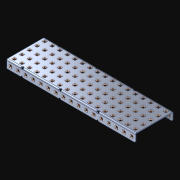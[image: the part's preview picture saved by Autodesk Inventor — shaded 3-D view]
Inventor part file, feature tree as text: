
AUTODESK INVENTOR PART (.ipt)
format: ipt  version: 2021 (Build 250183000, 183)  size: 1,876,480 bytes
history: native  units: in
note: dims shown in document units (in); Inventor stores cm internally (conversion verified against a paired STEP export)
features: extrude x120, other x120, sketch x4, pattern_linear x3
ambient origin geometry x8: Origin, YZ Plane, XZ Plane, XY Plane, X Axis, Y Axis, Z Axis, Center Point
bodies: Solid1 (feature_tree)
feature tree (247):
  pattern_linear  "Rectangular Pattern1"  Spacing1=0.182in  [1 undecoded]
  pattern_linear  "Rectangular Pattern2"  Spacing1=0.046in  [1 undecoded]
  pattern_linear  "Rectangular Pattern3"  Spacing1=0.5in  [1 undecoded]
  extrude  "Extrusion1"  Depth=0.046in
  sketch  "Sketch1"  dims[d0=0.182in]
  other  "Srf1"
  sketch  "Sketch2"  dims[d1=0.046in d2=0.0in]
  other  "Srf2"
  sketch  "Sketch3"  dims[d3=0.182in]
  other  "Srf3"
  other  "Srf4"
  other  "Srf5"
  other  "Srf6"
  other  "Srf7"
  other  "Srf8"
  other  "Srf9"
  other  "Srf10"
  other  "Srf11"
  other  "Srf12"
  other  "Srf13"
  other  "Srf14"
  other  "Srf15"
  other  "Srf16"
  other  "Srf17"
  other  "Srf18"
  other  "Srf19"
  other  "Srf38"
  other  "Srf39"
  other  "Srf40"
  other  "Srf41"
  other  "Srf42"
  other  "Srf43"
  other  "Srf44"
  other  "Srf45"
  other  "Srf46"
  other  "Srf47"
  other  "Srf48"
  other  "Srf49"
  other  "Srf50"
  other  "Srf51"
  other  "Srf52"
  other  "Srf53"
  other  "Srf72"
  other  "Srf73"
  other  "Srf74"
  other  "Srf75"
  other  "Srf76"
  other  "Srf77"
  other  "Srf78"
  other  "Srf79"
  other  "Srf80"
  other  "Srf81"
  other  "Srf82"
  other  "Srf83"
  other  "Srf84"
  other  "Srf85"
  other  "Srf86"
  other  "Srf87"
  other  "Srf88"
  other  "Srf107"
  other  "Srf108"
  other  "Srf109"
  other  "Srf110"
  other  "Srf111"
  other  "Srf112"
  other  "Srf113"
  other  "Srf114"
  other  "Srf115"
  other  "Srf116"
  other  "Srf117"
  other  "Srf118"
  other  "Srf119"
  other  "Srf120"
  other  "Srf121"
  other  "Srf122"
  other  "Srf123"
  other  "Srf142"
  other  "Srf143"
  other  "Srf144"
  other  "Srf145"
  other  "Srf146"
  other  "Srf147"
  other  "Srf148"
  other  "Srf149"
  other  "Srf150"
  other  "Srf151"
  other  "Srf152"
  other  "Srf153"
  other  "Srf154"
  other  "Srf155"
  other  "Srf156"
  other  "Srf157"
  other  "Srf158"
  other  "Srf177"
  other  "Srf178"
  other  "Srf179"
  other  "Srf180"
  other  "Srf181"
  other  "Srf182"
  other  "Srf183"
  other  "Srf184"
  other  "Srf185"
  other  "Srf186"
  other  "Srf187"
  other  "Srf188"
  other  "Srf189"
  other  "Srf190"
  other  "Srf191"
  other  "Srf192"
  other  "Srf193"
  other  "Srf212"
  other  "Srf213"
  other  "Srf214"
  other  "Srf215"
  other  "Srf216"
  other  "Srf217"
  other  "Srf218"
  other  "Srf219"
  other  "Srf220"
  other  "Srf221"
  other  "Srf222"
  other  "Srf223"
  other  "Srf224"
  other  "Srf225"
  other  "Srf226"
  other  "Srf227"
  sketch  "Sketch4"  dims[d4=0.046in d5=0.0in d6=0.182in d7=0.046in d8=0.0in d11=0.5in d12=6.6929in d14=0.5in d15=1.9685in d17=0.5in d18=6.6929in d20=0.5in d21=9.0in d22=0.0in]
  parser-record x1  (decoder bookkeeping rows leaked as tree rows — omitted from the tree; the rows remain in map.json)
  extrude  "ExtrusionSrf1"  Depth=0.046in
  extrude  "ExtrusionSrf2"  Depth=0.046in
  extrude  "ExtrusionSrf3"  Depth=0.046in
  extrude  "ExtrusionSrf4"  Depth=0.046in
  extrude  "ExtrusionSrf5"  Depth=0.046in
  extrude  "ExtrusionSrf6"  TaperAngle=0.0deg  [1 undecoded]
  extrude  "ExtrusionSrf7"  [1 undecoded]
  extrude  "ExtrusionSrf8"  [1 undecoded]
  extrude  "ExtrusionSrf9"  [1 undecoded]
  extrude  "ExtrusionSrf10"  [1 undecoded]
  extrude  "ExtrusionSrf11"  [1 undecoded]
  extrude  "ExtrusionSrf12"  [1 undecoded]
  extrude  "ExtrusionSrf13"  [1 undecoded]
  extrude  "ExtrusionSrf14"  [1 undecoded]
  extrude  "ExtrusionSrf15"  [1 undecoded]
  extrude  "ExtrusionSrf16"  [1 undecoded]
  extrude  "ExtrusionSrf17"  [1 undecoded]
  extrude  "ExtrusionSrf18"  [1 undecoded]
  extrude  "ExtrusionSrf19"  [1 undecoded]
  extrude  "ExtrusionSrf38"  [1 undecoded]
  extrude  "ExtrusionSrf39"  [1 undecoded]
  extrude  "ExtrusionSrf40"  [1 undecoded]
  extrude  "ExtrusionSrf41"  [1 undecoded]
  extrude  "ExtrusionSrf42"  [1 undecoded]
  extrude  "ExtrusionSrf43"  [1 undecoded]
  extrude  "ExtrusionSrf44"  [1 undecoded]
  extrude  "ExtrusionSrf45"  [1 undecoded]
  extrude  "ExtrusionSrf46"  [1 undecoded]
  extrude  "ExtrusionSrf47"  [1 undecoded]
  extrude  "ExtrusionSrf48"  [1 undecoded]
  extrude  "ExtrusionSrf49"  [1 undecoded]
  extrude  "ExtrusionSrf50"  [1 undecoded]
  extrude  "ExtrusionSrf51"  [1 undecoded]
  extrude  "ExtrusionSrf52"  [1 undecoded]
  extrude  "ExtrusionSrf53"  [1 undecoded]
  extrude  "ExtrusionSrf72"  [1 undecoded]
  extrude  "ExtrusionSrf73"  [1 undecoded]
  extrude  "ExtrusionSrf74"  [1 undecoded]
  extrude  "ExtrusionSrf75"  [1 undecoded]
  extrude  "ExtrusionSrf76"  [1 undecoded]
  extrude  "ExtrusionSrf77"  [1 undecoded]
  extrude  "ExtrusionSrf78"  [1 undecoded]
  extrude  "ExtrusionSrf79"  [1 undecoded]
  extrude  "ExtrusionSrf80"  [1 undecoded]
  extrude  "ExtrusionSrf81"  [1 undecoded]
  extrude  "ExtrusionSrf82"  [1 undecoded]
  extrude  "ExtrusionSrf83"  [1 undecoded]
  extrude  "ExtrusionSrf84"  [1 undecoded]
  extrude  "ExtrusionSrf85"  [1 undecoded]
  extrude  "ExtrusionSrf86"  [1 undecoded]
  extrude  "ExtrusionSrf87"  [1 undecoded]
  extrude  "ExtrusionSrf88"  [1 undecoded]
  extrude  "ExtrusionSrf107"  [1 undecoded]
  extrude  "ExtrusionSrf108"  [1 undecoded]
  extrude  "ExtrusionSrf109"  [1 undecoded]
  extrude  "ExtrusionSrf110"  [1 undecoded]
  extrude  "ExtrusionSrf111"  [1 undecoded]
  extrude  "ExtrusionSrf112"  [1 undecoded]
  extrude  "ExtrusionSrf113"  [1 undecoded]
  extrude  "ExtrusionSrf114"  [1 undecoded]
  extrude  "ExtrusionSrf115"  [1 undecoded]
  extrude  "ExtrusionSrf116"  [1 undecoded]
  extrude  "ExtrusionSrf117"  [1 undecoded]
  extrude  "ExtrusionSrf118"  [1 undecoded]
  extrude  "ExtrusionSrf119"  [1 undecoded]
  extrude  "ExtrusionSrf120"  [1 undecoded]
  extrude  "ExtrusionSrf121"  [1 undecoded]
  extrude  "ExtrusionSrf122"  [1 undecoded]
  extrude  "ExtrusionSrf123"  [1 undecoded]
  extrude  "ExtrusionSrf142"  [1 undecoded]
  extrude  "ExtrusionSrf143"  [1 undecoded]
  extrude  "ExtrusionSrf144"  [1 undecoded]
  extrude  "ExtrusionSrf145"  [1 undecoded]
  extrude  "ExtrusionSrf146"  [1 undecoded]
  extrude  "ExtrusionSrf147"  [1 undecoded]
  extrude  "ExtrusionSrf148"  [1 undecoded]
  extrude  "ExtrusionSrf149"  [1 undecoded]
  extrude  "ExtrusionSrf150"  [1 undecoded]
  extrude  "ExtrusionSrf151"  [1 undecoded]
  extrude  "ExtrusionSrf152"  [1 undecoded]
  extrude  "ExtrusionSrf153"  [1 undecoded]
  extrude  "ExtrusionSrf154"  [1 undecoded]
  extrude  "ExtrusionSrf155"  [1 undecoded]
  extrude  "ExtrusionSrf156"  [1 undecoded]
  extrude  "ExtrusionSrf157"  [1 undecoded]
  extrude  "ExtrusionSrf158"  [1 undecoded]
  extrude  "ExtrusionSrf177"  [1 undecoded]
  extrude  "ExtrusionSrf178"  [1 undecoded]
  extrude  "ExtrusionSrf179"  [1 undecoded]
  extrude  "ExtrusionSrf180"  [1 undecoded]
  extrude  "ExtrusionSrf181"  [1 undecoded]
  extrude  "ExtrusionSrf182"  [1 undecoded]
  extrude  "ExtrusionSrf183"  [1 undecoded]
  extrude  "ExtrusionSrf184"  [1 undecoded]
  extrude  "ExtrusionSrf185"  [1 undecoded]
  extrude  "ExtrusionSrf186"  [1 undecoded]
  extrude  "ExtrusionSrf187"  [1 undecoded]
  extrude  "ExtrusionSrf188"  [1 undecoded]
  extrude  "ExtrusionSrf189"  [1 undecoded]
  extrude  "ExtrusionSrf190"  [1 undecoded]
  extrude  "ExtrusionSrf191"  [1 undecoded]
  extrude  "ExtrusionSrf192"  [1 undecoded]
  extrude  "ExtrusionSrf193"  [1 undecoded]
  extrude  "ExtrusionSrf212"  [1 undecoded]
  extrude  "ExtrusionSrf213"  [1 undecoded]
  extrude  "ExtrusionSrf214"  [1 undecoded]
  extrude  "ExtrusionSrf215"  [1 undecoded]
  extrude  "ExtrusionSrf216"  [1 undecoded]
  extrude  "ExtrusionSrf217"  [1 undecoded]
  extrude  "ExtrusionSrf218"  [1 undecoded]
  extrude  "ExtrusionSrf219"  [1 undecoded]
  extrude  "ExtrusionSrf220"  [1 undecoded]
  extrude  "ExtrusionSrf221"  [1 undecoded]
  extrude  "ExtrusionSrf222"  [1 undecoded]
  extrude  "ExtrusionSrf223"  [1 undecoded]
  extrude  "ExtrusionSrf224"  [1 undecoded]
  extrude  "ExtrusionSrf225"  [1 undecoded]
  extrude  "ExtrusionSrf226"  [1 undecoded]
  extrude  "ExtrusionSrf227"  [1 undecoded]
note: 117 required parameter values undecoded (feature->parameter linkage not recoverable at this tier; creation-order binding heuristic only, values carry confidence <= 0.55)
